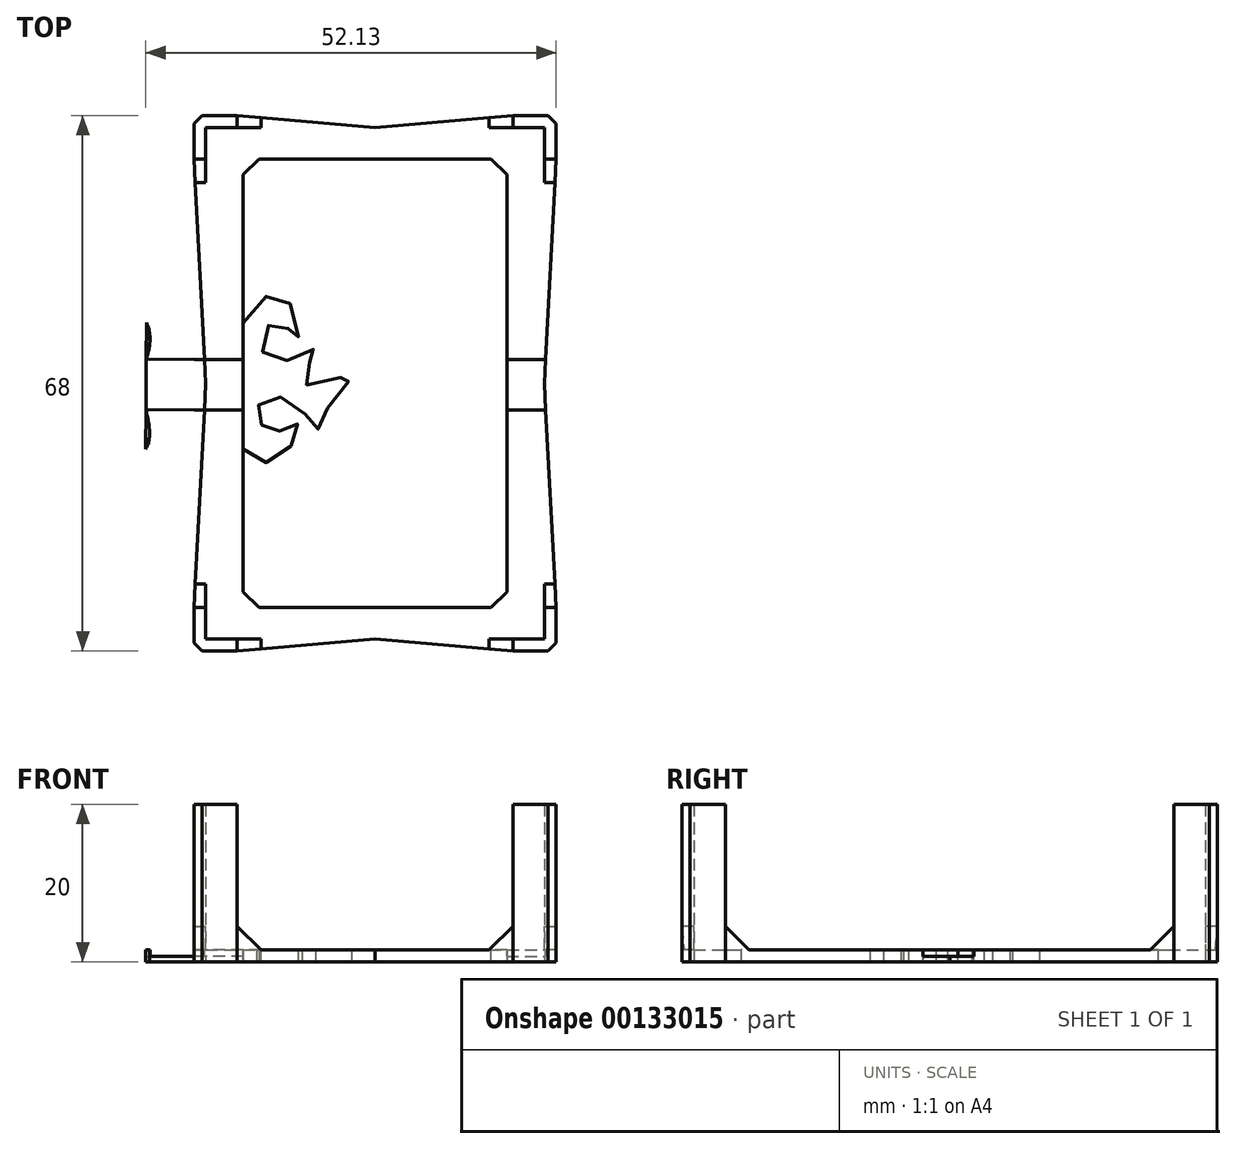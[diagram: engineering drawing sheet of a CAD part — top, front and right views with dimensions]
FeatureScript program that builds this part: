
annotation { "Feature Type Name" : "Feature", "Feature Type Description" : "" }
export const myFeature = defineFeature(function(context is Context, id is Id, definition is map)
    precondition{}
    {
        {
            var Q0;
            Q0=qCreatedBy(makeId("Top.planeOp"),FACE);
            var sketch = newSketch(context, id + "F0", { "sketchPlane" : qUnion([Q0])});
            skLineSegment(sketch, "E0.bottom", {"start": v(21.5, 32.5) * mm, "end": v(17.5, 32.5) * mm});
            skLineSegment(sketch, "E0.top", {"start": v(21.5, -32.5) * mm, "end": v(17.5, -32.5) * mm});
            skLineSegment(sketch, "E0.left", {"start": v(21.5, 32.5) * mm, "end": v(21.5, 28.5) * mm});
            skLineSegment(sketch, "E0.right", {"start": v(-21.5, 32.5) * mm, "end": v(-21.5, 28.5) * mm});
            skLineSegment(sketch, "E1", {"start": v(-17.5, 34) * mm, "end": v(-23, 34) * mm});
            skLineSegment(sketch, "E2", {"start": v(-23, 34) * mm, "end": v(-23, 28.5) * mm});
            skLineSegment(sketch, "E3", {"start": v(-17.5, 32.5) * mm, "end": v(-17.5, 34) * mm});
            skLineSegment(sketch, "E4", {"start": v(-21.5, 28.5) * mm, "end": v(-23, 28.5) * mm});
            skLineSegment(sketch, "E5", {"start": v(17.5, 34) * mm, "end": v(17.5, 32.5) * mm});
            skLineSegment(sketch, "E6", {"start": v(17.5, 34) * mm, "end": v(23, 34) * mm});
            skLineSegment(sketch, "E7", {"start": v(23, 28.5) * mm, "end": v(23, 34) * mm});
            skLineSegment(sketch, "E8", {"start": v(21.5, 28.5) * mm, "end": v(23, 28.5) * mm});
            skLineSegment(sketch, "E9", {"start": v(-23, -28.5) * mm, "end": v(-21.5, -28.5) * mm});
            skLineSegment(sketch, "E10", {"start": v(-23, -28.5) * mm, "end": v(-23, -34) * mm});
            skLineSegment(sketch, "E11", {"start": v(-17.5, -34) * mm, "end": v(-23, -34) * mm});
            skLineSegment(sketch, "E12", {"start": v(-17.5, -32.5) * mm, "end": v(-17.5, -34) * mm});
            skLineSegment(sketch, "E13", {"start": v(17.5, -32.5) * mm, "end": v(17.5, -34) * mm});
            skLineSegment(sketch, "E14", {"start": v(17.5, -34) * mm, "end": v(23, -34) * mm});
            skLineSegment(sketch, "E15", {"start": v(23, -28.5) * mm, "end": v(23, -34) * mm});
            skLineSegment(sketch, "E16", {"start": v(21.5, -28.5) * mm, "end": v(23, -28.5) * mm});
            skLineSegment(sketch, "E17", {"start": v(-16.75, 28.5) * mm, "end": v(16.75, 28.5) * mm});
            skLineSegment(sketch, "E18", {"start": v(16.75, -28.5) * mm, "end": v(-16.75, -28.5) * mm});
            skLineSegment(sketch, "E19", {"start": v(-16.75, 28.5) * mm, "end": v(-16.75, -28.5) * mm});
            skLineSegment(sketch, "E20", {"start": v(16.75, 28.5) * mm, "end": v(16.75, -28.5) * mm});
            skLineSegment(sketch, "E21", {"start": v(-23, 28.5) * mm, "end": v(-21.5, 0) * mm});
            skLineSegment(sketch, "E22", {"start": v(-21.5, 0) * mm, "end": v(-23, -28.5) * mm});
            skLineSegment(sketch, "E23", {"start": v(23, -28.5) * mm, "end": v(21.5, 0) * mm});
            skLineSegment(sketch, "E24", {"start": v(23, 28.5) * mm, "end": v(21.5, 0) * mm});
            skLineSegment(sketch, "E25", {"start": v(-17.5, 34) * mm, "end": v(0, 32.5) * mm});
            skLineSegment(sketch, "E26", {"start": v(0, 32.5) * mm, "end": v(17.5, 34) * mm});
            skLineSegment(sketch, "E27", {"start": v(-17.5, -34) * mm, "end": v(0, -32.5) * mm});
            skLineSegment(sketch, "E28", {"start": v(0, -32.5) * mm, "end": v(17.5, -34) * mm});
            skLineSegment(sketch, "E29.trimOffspring", {"start": v(21.5, -28.5) * mm, "end": v(21.5, -32.5) * mm});
            skLineSegment(sketch, "E30.trimOffspring", {"start": v(-17.5, -32.5) * mm, "end": v(-21.5, -32.5) * mm});
            skLineSegment(sketch, "E31.trimOffspring", {"start": v(-21.5, -28.5) * mm, "end": v(-21.5, -32.5) * mm});
            skLineSegment(sketch, "E32", {"start": v(-17.5, 32.5) * mm, "end": v(-21.5, 32.5) * mm});
            skPoint(sketch, "E33", {"position": v(0, 28.5) * mm});
            skPoint(sketch, "E34", {"position": v(0, -28.5) * mm});
            skPoint(sketch, "E35", {"position": v(-16.75, 0) * mm});
            skPoint(sketch, "E36", {"position": v(16.75, 0) * mm});
            skSolve(sketch);
        }
        {
            var Q0;
            {var subQ0=sQuery(id+"F0.wireOp",EDGE,"E0.left");var subQ3=sQuery(id+"F0.wireOp",EDGE,"E0.bottom");var subQ4=makeQuery(id+"F0.imprint","INTERSECT",VERTEX,{"derivedFrom":[subQ3,subQ0]});Q0=makeQuery(id+"F0.imprint","IMPRINT",FACE,{"disambiguationData":[TD([[makeQuery(id+"F0.imprint","IMPRINT",EDGE,{"disambiguationData":[TD([[subQ4,-1.0]])],"derivedFrom":subQ3}),1.0]])]});}
            var Q1;
            {var subQ0=sQuery(id+"F0.wireOp",EDGE,"E5");Q1=makeQuery(id+"F0.imprint","IMPRINT",FACE,{"disambiguationData":[TD([[makeQuery(id+"F0.imprint","IMPRINT",EDGE,{"derivedFrom":subQ0}),-1.0]])]});}
            var Q2;
            {var subQ4=sQuery(id+"F0.wireOp",EDGE,"E5");Q2=makeQuery(id+"F0.imprint","IMPRINT",FACE,{"disambiguationData":[TD([[makeQuery(id+"F0.imprint","IMPRINT",EDGE,{"derivedFrom":subQ4}),1.0]])]});}
            var Q3;
            {var subQ0=sQuery(id+"F0.wireOp",EDGE,"E8");Q3=makeQuery(id+"F0.imprint","IMPRINT",FACE,{"disambiguationData":[TD([[makeQuery(id+"F0.imprint","IMPRINT",EDGE,{"derivedFrom":subQ0}),-1.0]])]});}
            var Q4;
            {var subQ0=sQuery(id+"F0.wireOp",EDGE,"E16");Q4=makeQuery(id+"F0.imprint","IMPRINT",FACE,{"disambiguationData":[TD([[makeQuery(id+"F0.imprint","IMPRINT",EDGE,{"derivedFrom":subQ0}),1.0]])]});}
            var Q5;
            {var subQ0=sQuery(id+"F0.wireOp",EDGE,"E13");Q5=makeQuery(id+"F0.imprint","IMPRINT",FACE,{"disambiguationData":[TD([[makeQuery(id+"F0.imprint","IMPRINT",EDGE,{"derivedFrom":subQ0}),1.0]])]});}
            var Q6;
            {var subQ0=sQuery(id+"F0.wireOp",EDGE,"E13");Q6=makeQuery(id+"F0.imprint","IMPRINT",FACE,{"disambiguationData":[TD([[makeQuery(id+"F0.imprint","IMPRINT",EDGE,{"derivedFrom":subQ0}),-1.0]])]});}
            var Q7;
            {var subQ0=sQuery(id+"F0.wireOp",EDGE,"E12");Q7=makeQuery(id+"F0.imprint","IMPRINT",FACE,{"disambiguationData":[TD([[makeQuery(id+"F0.imprint","IMPRINT",EDGE,{"derivedFrom":subQ0}),1.0]])]});}
            var Q8;
            {var subQ4=sQuery(id+"F0.wireOp",EDGE,"E9");Q8=makeQuery(id+"F0.imprint","IMPRINT",FACE,{"disambiguationData":[TD([[makeQuery(id+"F0.imprint","IMPRINT",EDGE,{"derivedFrom":subQ4}),-1.0]])]});}
            var Q9;
            {var subQ0=sQuery(id+"F0.wireOp",EDGE,"E9");Q9=makeQuery(id+"F0.imprint","IMPRINT",FACE,{"disambiguationData":[TD([[makeQuery(id+"F0.imprint","IMPRINT",EDGE,{"derivedFrom":subQ0}),1.0]])]});}
            var Q10;
            {var subQ0=sQuery(id+"F0.wireOp",EDGE,"E4");Q10=makeQuery(id+"F0.imprint","IMPRINT",FACE,{"disambiguationData":[TD([[makeQuery(id+"F0.imprint","IMPRINT",EDGE,{"derivedFrom":subQ0}),1.0]])]});}
            var Q11;
            Q11=makeQuery(id+"F0.imprint","IMPRINT",FACE,{"disambiguationData":[TD([[makeQuery(id+"F0.imprint","IMPRINT",EDGE,{"derivedFrom":sQuery(id+"F0.wireOp",EDGE,"E1")}),1.0]])]});
            var Q12;
            {var subQ0=sQuery(id+"F0.wireOp",EDGE,"E3");Q12=makeQuery(id+"F0.imprint","IMPRINT",FACE,{"disambiguationData":[TD([[makeQuery(id+"F0.imprint","IMPRINT",EDGE,{"derivedFrom":subQ0}),-1.0]])]});}
            extrude(context, id + "F1", {"entities" : qUnion([Q0, Q1, Q2, Q3, Q4, Q5, Q6, Q7, Q8, Q9, Q10, Q11, Q12]), "depth" : 1.5 * mm});
        }
        {
            var Q0;
            Q0=makeQuery(id+"F0.imprint","IMPRINT",FACE,{"disambiguationData":[TD([[makeQuery(id+"F0.imprint","IMPRINT",EDGE,{"derivedFrom":sQuery(id+"F0.wireOp",EDGE,"E1")}),1.0]])]});
            var Q1;
            {var subQ4=sQuery(id+"F0.wireOp",EDGE,"E5");Q1=makeQuery(id+"F0.imprint","IMPRINT",FACE,{"disambiguationData":[TD([[makeQuery(id+"F0.imprint","IMPRINT",EDGE,{"derivedFrom":subQ4}),1.0]])]});}
            var Q2;
            {var subQ0=sQuery(id+"F0.wireOp",EDGE,"E13");Q2=makeQuery(id+"F0.imprint","IMPRINT",FACE,{"disambiguationData":[TD([[makeQuery(id+"F0.imprint","IMPRINT",EDGE,{"derivedFrom":subQ0}),1.0]])]});}
            var Q3;
            {var subQ3=sQuery(id+"F0.wireOp",EDGE,"E9");Q3=makeQuery(id+"F0.imprint","IMPRINT",FACE,{"disambiguationData":[TD([[makeQuery(id+"F0.imprint","IMPRINT",EDGE,{"derivedFrom":subQ3}),-1.0]])]});}
            extrude(context, id + "F2", {"entities" : qUnion([Q0, Q1, Q2, Q3]), "operationType" : NewBodyOperationType.ADD, "depth" : 20 * mm});
        }
        {
            var Q0;
            Q0=makeQuery(id+"F2.boolean.opBoolean","INTERSECT",EDGE,{"derivedFrom":[makeQuery(id+"F1.opExtrude","CAP_FACE",FACE,{"disambiguationData":[OSD([sQuery(id+"F0.wireOp",EDGE,"E1"),sQuery(id+"F0.wireOp",EDGE,"E2"),sQuery(id+"F0.wireOp",EDGE,"E6"),sQuery(id+"F0.wireOp",EDGE,"E7"),sQuery(id+"F0.wireOp",EDGE,"E10"),sQuery(id+"F0.wireOp",EDGE,"E11"),sQuery(id+"F0.wireOp",EDGE,"E14"),sQuery(id+"F0.wireOp",EDGE,"E15"),sQuery(id+"F0.wireOp",EDGE,"E17"),sQuery(id+"F0.wireOp",EDGE,"E18"),sQuery(id+"F0.wireOp",EDGE,"E19"),sQuery(id+"F0.wireOp",EDGE,"E20"),sQuery(id+"F0.wireOp",EDGE,"E21"),sQuery(id+"F0.wireOp",EDGE,"E22"),sQuery(id+"F0.wireOp",EDGE,"E23"),sQuery(id+"F0.wireOp",EDGE,"E24"),sQuery(id+"F0.wireOp",EDGE,"E25"),sQuery(id+"F0.wireOp",EDGE,"E26"),sQuery(id+"F0.wireOp",EDGE,"E27"),sQuery(id+"F0.wireOp",EDGE,"E28")])],"isStart":false}),makeQuery(id+"F2.opExtrude","SWEPT_FACE",FACE,{"disambiguationData":[OSD([sQuery(id+"F0.wireOp",EDGE,"E4")])]})]});
            var Q1;
            Q1=makeQuery(id+"F2.boolean.opBoolean","INTERSECT",EDGE,{"derivedFrom":[makeQuery(id+"F1.opExtrude","CAP_FACE",FACE,{"disambiguationData":[OSD([sQuery(id+"F0.wireOp",EDGE,"E1"),sQuery(id+"F0.wireOp",EDGE,"E2"),sQuery(id+"F0.wireOp",EDGE,"E6"),sQuery(id+"F0.wireOp",EDGE,"E7"),sQuery(id+"F0.wireOp",EDGE,"E10"),sQuery(id+"F0.wireOp",EDGE,"E11"),sQuery(id+"F0.wireOp",EDGE,"E14"),sQuery(id+"F0.wireOp",EDGE,"E15"),sQuery(id+"F0.wireOp",EDGE,"E17"),sQuery(id+"F0.wireOp",EDGE,"E18"),sQuery(id+"F0.wireOp",EDGE,"E19"),sQuery(id+"F0.wireOp",EDGE,"E20"),sQuery(id+"F0.wireOp",EDGE,"E21"),sQuery(id+"F0.wireOp",EDGE,"E22"),sQuery(id+"F0.wireOp",EDGE,"E23"),sQuery(id+"F0.wireOp",EDGE,"E24"),sQuery(id+"F0.wireOp",EDGE,"E25"),sQuery(id+"F0.wireOp",EDGE,"E26"),sQuery(id+"F0.wireOp",EDGE,"E27"),sQuery(id+"F0.wireOp",EDGE,"E28")])],"isStart":false}),makeQuery(id+"F2.opExtrude","SWEPT_FACE",FACE,{"disambiguationData":[OSD([sQuery(id+"F0.wireOp",EDGE,"E3")])]})]});
            var Q2;
            Q2=makeQuery(id+"F2.boolean.opBoolean","INTERSECT",EDGE,{"derivedFrom":[makeQuery(id+"F1.opExtrude","CAP_FACE",FACE,{"disambiguationData":[OSD([sQuery(id+"F0.wireOp",EDGE,"E1"),sQuery(id+"F0.wireOp",EDGE,"E2"),sQuery(id+"F0.wireOp",EDGE,"E6"),sQuery(id+"F0.wireOp",EDGE,"E7"),sQuery(id+"F0.wireOp",EDGE,"E10"),sQuery(id+"F0.wireOp",EDGE,"E11"),sQuery(id+"F0.wireOp",EDGE,"E14"),sQuery(id+"F0.wireOp",EDGE,"E15"),sQuery(id+"F0.wireOp",EDGE,"E17"),sQuery(id+"F0.wireOp",EDGE,"E18"),sQuery(id+"F0.wireOp",EDGE,"E19"),sQuery(id+"F0.wireOp",EDGE,"E20"),sQuery(id+"F0.wireOp",EDGE,"E21"),sQuery(id+"F0.wireOp",EDGE,"E22"),sQuery(id+"F0.wireOp",EDGE,"E23"),sQuery(id+"F0.wireOp",EDGE,"E24"),sQuery(id+"F0.wireOp",EDGE,"E25"),sQuery(id+"F0.wireOp",EDGE,"E26"),sQuery(id+"F0.wireOp",EDGE,"E27"),sQuery(id+"F0.wireOp",EDGE,"E28")])],"isStart":false}),makeQuery(id+"F2.opExtrude","SWEPT_FACE",FACE,{"disambiguationData":[OSD([sQuery(id+"F0.wireOp",EDGE,"E8")])]})]});
            var Q3;
            Q3=makeQuery(id+"F2.boolean.opBoolean","INTERSECT",EDGE,{"derivedFrom":[makeQuery(id+"F1.opExtrude","CAP_FACE",FACE,{"disambiguationData":[OSD([sQuery(id+"F0.wireOp",EDGE,"E1"),sQuery(id+"F0.wireOp",EDGE,"E2"),sQuery(id+"F0.wireOp",EDGE,"E6"),sQuery(id+"F0.wireOp",EDGE,"E7"),sQuery(id+"F0.wireOp",EDGE,"E10"),sQuery(id+"F0.wireOp",EDGE,"E11"),sQuery(id+"F0.wireOp",EDGE,"E14"),sQuery(id+"F0.wireOp",EDGE,"E15"),sQuery(id+"F0.wireOp",EDGE,"E17"),sQuery(id+"F0.wireOp",EDGE,"E18"),sQuery(id+"F0.wireOp",EDGE,"E19"),sQuery(id+"F0.wireOp",EDGE,"E20"),sQuery(id+"F0.wireOp",EDGE,"E21"),sQuery(id+"F0.wireOp",EDGE,"E22"),sQuery(id+"F0.wireOp",EDGE,"E23"),sQuery(id+"F0.wireOp",EDGE,"E24"),sQuery(id+"F0.wireOp",EDGE,"E25"),sQuery(id+"F0.wireOp",EDGE,"E26"),sQuery(id+"F0.wireOp",EDGE,"E27"),sQuery(id+"F0.wireOp",EDGE,"E28")])],"isStart":false}),makeQuery(id+"F2.opExtrude","SWEPT_FACE",FACE,{"disambiguationData":[OSD([sQuery(id+"F0.wireOp",EDGE,"E5")])]})]});
            var Q4;
            Q4=makeQuery(id+"F2.boolean.opBoolean","INTERSECT",EDGE,{"derivedFrom":[makeQuery(id+"F1.opExtrude","CAP_FACE",FACE,{"disambiguationData":[OSD([sQuery(id+"F0.wireOp",EDGE,"E1"),sQuery(id+"F0.wireOp",EDGE,"E2"),sQuery(id+"F0.wireOp",EDGE,"E6"),sQuery(id+"F0.wireOp",EDGE,"E7"),sQuery(id+"F0.wireOp",EDGE,"E10"),sQuery(id+"F0.wireOp",EDGE,"E11"),sQuery(id+"F0.wireOp",EDGE,"E14"),sQuery(id+"F0.wireOp",EDGE,"E15"),sQuery(id+"F0.wireOp",EDGE,"E17"),sQuery(id+"F0.wireOp",EDGE,"E18"),sQuery(id+"F0.wireOp",EDGE,"E19"),sQuery(id+"F0.wireOp",EDGE,"E20"),sQuery(id+"F0.wireOp",EDGE,"E21"),sQuery(id+"F0.wireOp",EDGE,"E22"),sQuery(id+"F0.wireOp",EDGE,"E23"),sQuery(id+"F0.wireOp",EDGE,"E24"),sQuery(id+"F0.wireOp",EDGE,"E25"),sQuery(id+"F0.wireOp",EDGE,"E26"),sQuery(id+"F0.wireOp",EDGE,"E27"),sQuery(id+"F0.wireOp",EDGE,"E28")])],"isStart":false}),makeQuery(id+"F2.opExtrude","SWEPT_FACE",FACE,{"disambiguationData":[OSD([sQuery(id+"F0.wireOp",EDGE,"E12")])]})]});
            var Q5;
            Q5=makeQuery(id+"F2.boolean.opBoolean","INTERSECT",EDGE,{"derivedFrom":[makeQuery(id+"F1.opExtrude","CAP_FACE",FACE,{"disambiguationData":[OSD([sQuery(id+"F0.wireOp",EDGE,"E1"),sQuery(id+"F0.wireOp",EDGE,"E2"),sQuery(id+"F0.wireOp",EDGE,"E6"),sQuery(id+"F0.wireOp",EDGE,"E7"),sQuery(id+"F0.wireOp",EDGE,"E10"),sQuery(id+"F0.wireOp",EDGE,"E11"),sQuery(id+"F0.wireOp",EDGE,"E14"),sQuery(id+"F0.wireOp",EDGE,"E15"),sQuery(id+"F0.wireOp",EDGE,"E17"),sQuery(id+"F0.wireOp",EDGE,"E18"),sQuery(id+"F0.wireOp",EDGE,"E19"),sQuery(id+"F0.wireOp",EDGE,"E20"),sQuery(id+"F0.wireOp",EDGE,"E21"),sQuery(id+"F0.wireOp",EDGE,"E22"),sQuery(id+"F0.wireOp",EDGE,"E23"),sQuery(id+"F0.wireOp",EDGE,"E24"),sQuery(id+"F0.wireOp",EDGE,"E25"),sQuery(id+"F0.wireOp",EDGE,"E26"),sQuery(id+"F0.wireOp",EDGE,"E27"),sQuery(id+"F0.wireOp",EDGE,"E28")])],"isStart":false}),makeQuery(id+"F2.opExtrude","SWEPT_FACE",FACE,{"disambiguationData":[OSD([sQuery(id+"F0.wireOp",EDGE,"E9")])]})]});
            var Q6;
            Q6=makeQuery(id+"F2.boolean.opBoolean","INTERSECT",EDGE,{"derivedFrom":[makeQuery(id+"F1.opExtrude","CAP_FACE",FACE,{"disambiguationData":[OSD([sQuery(id+"F0.wireOp",EDGE,"E1"),sQuery(id+"F0.wireOp",EDGE,"E2"),sQuery(id+"F0.wireOp",EDGE,"E6"),sQuery(id+"F0.wireOp",EDGE,"E7"),sQuery(id+"F0.wireOp",EDGE,"E10"),sQuery(id+"F0.wireOp",EDGE,"E11"),sQuery(id+"F0.wireOp",EDGE,"E14"),sQuery(id+"F0.wireOp",EDGE,"E15"),sQuery(id+"F0.wireOp",EDGE,"E17"),sQuery(id+"F0.wireOp",EDGE,"E18"),sQuery(id+"F0.wireOp",EDGE,"E19"),sQuery(id+"F0.wireOp",EDGE,"E20"),sQuery(id+"F0.wireOp",EDGE,"E21"),sQuery(id+"F0.wireOp",EDGE,"E22"),sQuery(id+"F0.wireOp",EDGE,"E23"),sQuery(id+"F0.wireOp",EDGE,"E24"),sQuery(id+"F0.wireOp",EDGE,"E25"),sQuery(id+"F0.wireOp",EDGE,"E26"),sQuery(id+"F0.wireOp",EDGE,"E27"),sQuery(id+"F0.wireOp",EDGE,"E28")])],"isStart":false}),makeQuery(id+"F2.opExtrude","SWEPT_FACE",FACE,{"disambiguationData":[OSD([sQuery(id+"F0.wireOp",EDGE,"E16")])]})]});
            var Q7;
            Q7=makeQuery(id+"F2.boolean.opBoolean","INTERSECT",EDGE,{"derivedFrom":[makeQuery(id+"F1.opExtrude","CAP_FACE",FACE,{"disambiguationData":[OSD([sQuery(id+"F0.wireOp",EDGE,"E1"),sQuery(id+"F0.wireOp",EDGE,"E2"),sQuery(id+"F0.wireOp",EDGE,"E6"),sQuery(id+"F0.wireOp",EDGE,"E7"),sQuery(id+"F0.wireOp",EDGE,"E10"),sQuery(id+"F0.wireOp",EDGE,"E11"),sQuery(id+"F0.wireOp",EDGE,"E14"),sQuery(id+"F0.wireOp",EDGE,"E15"),sQuery(id+"F0.wireOp",EDGE,"E17"),sQuery(id+"F0.wireOp",EDGE,"E18"),sQuery(id+"F0.wireOp",EDGE,"E19"),sQuery(id+"F0.wireOp",EDGE,"E20"),sQuery(id+"F0.wireOp",EDGE,"E21"),sQuery(id+"F0.wireOp",EDGE,"E22"),sQuery(id+"F0.wireOp",EDGE,"E23"),sQuery(id+"F0.wireOp",EDGE,"E24"),sQuery(id+"F0.wireOp",EDGE,"E25"),sQuery(id+"F0.wireOp",EDGE,"E26"),sQuery(id+"F0.wireOp",EDGE,"E27"),sQuery(id+"F0.wireOp",EDGE,"E28")])],"isStart":false}),makeQuery(id+"F2.opExtrude","SWEPT_FACE",FACE,{"disambiguationData":[OSD([sQuery(id+"F0.wireOp",EDGE,"E13")])]})]});
            chamfer(context, id + "F3", {"entities" : qUnion([Q0, Q1, Q2, Q3, Q4, Q5, Q6, Q7]), "width" : 3 * mm, "tangentPropagation" : true});
        }
        {
            var Q0;
            Q0=makeQuery(id+"F1.opExtrude","SWEPT_EDGE",EDGE,{"disambiguationData":[OSD([sQuery(id+"F0.wireOp",EDGE,"E17"),sQuery(id+"F0.wireOp",EDGE,"E19")])]});
            var Q1;
            Q1=makeQuery(id+"F1.opExtrude","SWEPT_EDGE",EDGE,{"disambiguationData":[OSD([sQuery(id+"F0.wireOp",EDGE,"E17"),sQuery(id+"F0.wireOp",EDGE,"E20")])]});
            var Q2;
            Q2=makeQuery(id+"F1.opExtrude","SWEPT_EDGE",EDGE,{"disambiguationData":[OSD([sQuery(id+"F0.wireOp",EDGE,"E18"),sQuery(id+"F0.wireOp",EDGE,"E19")])]});
            var Q3;
            Q3=makeQuery(id+"F1.opExtrude","SWEPT_EDGE",EDGE,{"disambiguationData":[OSD([sQuery(id+"F0.wireOp",EDGE,"E18"),sQuery(id+"F0.wireOp",EDGE,"E20")])]});
            chamfer(context, id + "F4", {"entities" : qUnion([Q0, Q1, Q2, Q3]), "width" : 2 * mm, "tangentPropagation" : true});
        }
        {
            var Q0;
            {var subQ0=sQuery(id+"F0.wireOp",EDGE,"E2");var subQ1=sQuery(id+"F0.wireOp",EDGE,"E1");Q0=makeQuery(id+"F2.boolean.opBoolean","MERGE",EDGE,{"derivedFrom":[makeQuery(id+"F1.opExtrude","SWEPT_EDGE",EDGE,{"disambiguationData":[OSD([subQ1,subQ0])]}),makeQuery(id+"F2.opExtrude","SWEPT_EDGE",EDGE,{"disambiguationData":[OSD([subQ1,subQ0])]})]});}
            var Q1;
            {var subQ0=sQuery(id+"F0.wireOp",EDGE,"E11");var subQ1=sQuery(id+"F0.wireOp",EDGE,"E10");Q1=makeQuery(id+"F2.boolean.opBoolean","MERGE",EDGE,{"derivedFrom":[makeQuery(id+"F1.opExtrude","SWEPT_EDGE",EDGE,{"disambiguationData":[OSD([subQ1,subQ0])]}),makeQuery(id+"F2.opExtrude","SWEPT_EDGE",EDGE,{"disambiguationData":[OSD([subQ1,subQ0])]})]});}
            var Q2;
            {var subQ0=sQuery(id+"F0.wireOp",EDGE,"E15");var subQ1=sQuery(id+"F0.wireOp",EDGE,"E14");Q2=makeQuery(id+"F2.boolean.opBoolean","MERGE",EDGE,{"derivedFrom":[makeQuery(id+"F1.opExtrude","SWEPT_EDGE",EDGE,{"disambiguationData":[OSD([subQ1,subQ0])]}),makeQuery(id+"F2.opExtrude","SWEPT_EDGE",EDGE,{"disambiguationData":[OSD([subQ1,subQ0])]})]});}
            var Q3;
            {var subQ0=sQuery(id+"F0.wireOp",EDGE,"E7");var subQ1=sQuery(id+"F0.wireOp",EDGE,"E6");Q3=makeQuery(id+"F2.boolean.opBoolean","MERGE",EDGE,{"derivedFrom":[makeQuery(id+"F1.opExtrude","SWEPT_EDGE",EDGE,{"disambiguationData":[OSD([subQ1,subQ0])]}),makeQuery(id+"F2.opExtrude","SWEPT_EDGE",EDGE,{"disambiguationData":[OSD([subQ1,subQ0])]})]});}
            chamfer(context, id + "F5", {"entities" : qUnion([Q0, Q1, Q2, Q3]), "width" : 1 * mm, "tangentPropagation" : true});
        }
        {
            var Q0;
            Q0=makeQuery(id+"F1.opExtrude","CAP_FACE",FACE,{"disambiguationData":[OSD([sQuery(id+"F0.wireOp",EDGE,"E1"),sQuery(id+"F0.wireOp",EDGE,"E2"),sQuery(id+"F0.wireOp",EDGE,"E6"),sQuery(id+"F0.wireOp",EDGE,"E7"),sQuery(id+"F0.wireOp",EDGE,"E10"),sQuery(id+"F0.wireOp",EDGE,"E11"),sQuery(id+"F0.wireOp",EDGE,"E14"),sQuery(id+"F0.wireOp",EDGE,"E15"),sQuery(id+"F0.wireOp",EDGE,"E17"),sQuery(id+"F0.wireOp",EDGE,"E18"),sQuery(id+"F0.wireOp",EDGE,"E19"),sQuery(id+"F0.wireOp",EDGE,"E20"),sQuery(id+"F0.wireOp",EDGE,"E21"),sQuery(id+"F0.wireOp",EDGE,"E22"),sQuery(id+"F0.wireOp",EDGE,"E23"),sQuery(id+"F0.wireOp",EDGE,"E24"),sQuery(id+"F0.wireOp",EDGE,"E25"),sQuery(id+"F0.wireOp",EDGE,"E26"),sQuery(id+"F0.wireOp",EDGE,"E27"),sQuery(id+"F0.wireOp",EDGE,"E28")])],"isStart":false});
            var sketch = newSketch(context, id + "F6", { "sketchPlane" : qUnion([Q0])});
            skLineSegment(sketch, "E37", {"start": v(0, 0) * mm, "end": v(-67.35, 0) * mm, "construction": true});
            skLineSegment(sketch, "E38", {"start": v(-23, -28.5) * mm, "end": v(-22.84, 25.5) * mm, "construction": true});
            skLineSegment(sketch, "E39.bottom", {"start": v(-16.75, 3.04) * mm, "end": v(-22.9, 3.04) * mm});
            skLineSegment(sketch, "E39.top", {"start": v(-16.75, -3.39) * mm, "end": v(-22.93, -3.39) * mm});
            skLineSegment(sketch, "E39.left", {"start": v(-16.75, 3.04) * mm, "end": v(-16.75, -0.17) * mm});
            skLineSegment(sketch, "E40", {"start": v(-16.75, -0.17) * mm, "end": v(-16.75, -3.39) * mm});
            skFitSpline(sketch, "E41", {"points": [v(-16.75, 3.04) * mm, v(-16.75, 7.68) * mm, v(-11.73, 11.2) * mm, v(-9.84, 5.5) * mm, v(-12.3, 8) * mm, v(-14.41, 4.39) * mm, v(-10.19, 3.12) * mm, v(-7.48, 4.31) * mm, v(-9.08, 0) * mm, v(-3.07, 1.03) * mm, v(-5.72, -2.62) * mm, v(-7.36, -5.84) * mm, v(-10.45, -2.32) * mm, v(-14.66, -2.56) * mm, v(-14.37, -5.3) * mm, v(-11.92, -6.03) * mm, v(-9.8, -5.22) * mm, v(-12.4, -9.74) * mm, v(-16.75, -8.38) * mm, v(-16.75, -3.39) * mm], "startDerivative": vector(-21.57, 75.62) * mm, "endDerivative": vector(21.75, 96.77) * mm});
            skLineSegment(sketch, "E42", {"start": v(-16.75, 7.68) * mm, "end": v(-16.75, 3.04) * mm});
            skLineSegment(sketch, "E43", {"start": v(-16.75, -3.39) * mm, "end": v(-16.75, -8.38) * mm});
            skFitSpline(sketch, "E44.MirrorCS", {"points": [v(-29.07, 3.08) * mm, v(-29.04, 7.72) * mm, v(-34.04, 11.27) * mm, v(-35.96, 5.57) * mm, v(-33.5, 8.05) * mm, v(-31.4, 4.44) * mm, v(-35.63, 3.2) * mm, v(-38.32, 4.4) * mm, v(-36.75, 0.08) * mm, v(-42.76, 1.15) * mm, v(-40.13, -2.52) * mm, v(-38.5, -5.75) * mm, v(-35.4, -2.25) * mm, v(-31.19, -2.5) * mm, v(-31.5, -5.25) * mm, v(-33.94, -5.97) * mm, v(-36.07, -5.15) * mm, v(-33.48, -9.68) * mm, v(-29.13, -8.34) * mm, v(-29.1, -3.35) * mm], "startDerivative": vector(22, 75.5) * mm, "endDerivative": vector(-21.18, 96.9) * mm});
            skLineSegment(sketch, "E45.MirrorCS", {"start": v(-29.04, 7.72) * mm, "end": v(-29.07, 3.08) * mm});
            skLineSegment(sketch, "E46.MirrorCS", {"start": v(-29.07, 3.08) * mm, "end": v(-22.9, 3.04) * mm});
            skLineSegment(sketch, "E47.MirrorCS", {"start": v(-29.1, -3.35) * mm, "end": v(-22.93, -3.39) * mm});
            skLineSegment(sketch, "E48.MirrorCS", {"start": v(-29.1, -3.35) * mm, "end": v(-29.13, -8.34) * mm});
            skLineSegment(sketch, "E49", {"start": v(-29.07, 3.08) * mm, "end": v(-29.1, -3.35) * mm});
            skSolve(sketch);
        }
        {
            var Q0;
            Q0=makeQuery(id+"F6.imprint","IMPRINT",FACE,{"disambiguationData":[TD([[makeQuery(id+"F6.imprint","IMPRINT",EDGE,{"derivedFrom":sQuery(id+"F6.wireOp",EDGE,"E44.MirrorCS")}),1.0]])]});
            var Q1;
            {var subQ1=sQuery(id+"F6.wireOp",EDGE,"E39.left");Q1=makeQuery(id+"F6.imprint","IMPRINT",FACE,{"disambiguationData":[TD([[makeQuery(id+"F6.imprint","IMPRINT",EDGE,{"derivedFrom":subQ1}),-1.0]])]});}
            var Q2;
            {var subQ1=sQuery(id+"F6.wireOp",EDGE,"E46.MirrorCS");Q2=makeQuery(id+"F6.imprint","IMPRINT",FACE,{"disambiguationData":[TD([[makeQuery(id+"F6.imprint","IMPRINT",EDGE,{"derivedFrom":subQ1}),-1.0]])]});}
            var Q3;
            Q3=makeQuery(id+"F6.imprint","IMPRINT",FACE,{"disambiguationData":[TD([[makeQuery(id+"F6.imprint","IMPRINT",EDGE,{"derivedFrom":sQuery(id+"F6.wireOp",EDGE,"E39.left")}),1.0]])]});
            extrude(context, id + "F7", {"entities" : qUnion([Q0, Q1, Q2, Q3]), "oppositeDirection" : true, "depth" : 1.5 * mm});
        }
        {
            var Q0;
            {var subQ1=sQuery(id+"F6.wireOp",EDGE,"E46.MirrorCS");Q0=makeQuery(id+"F6.imprint","IMPRINT",FACE,{"disambiguationData":[TD([[makeQuery(id+"F6.imprint","IMPRINT",EDGE,{"derivedFrom":subQ1}),-1.0]])]});}
            var Q1;
            {var subQ6=sQuery(id+"F6.wireOp",EDGE,"E39.left");Q1=makeQuery(id+"F6.imprint","IMPRINT",FACE,{"disambiguationData":[TD([[makeQuery(id+"F6.imprint","IMPRINT",EDGE,{"derivedFrom":subQ6}),-1.0]])]});}
            extrude(context, id + "F8", {"entities" : qUnion([Q0, Q1]), "operationType" : NewBodyOperationType.REMOVE, "oppositeDirection" : true, "depth" : .8 * mm});
        }
        {
            var Q0;
            Q0=makeQuery(id+"F6.imprint","IMPRINT",FACE,{"disambiguationData":[TD([[makeQuery(id+"F6.imprint","IMPRINT",EDGE,{"derivedFrom":sQuery(id+"F6.wireOp",EDGE,"E44.MirrorCS")}),1.0]])]});
            var sketch = newSketch(context, id + "F9", { "sketchPlane" : qUnion([Q0])});
            skLineSegment(sketch, "E50.0.0", {"start": v(-21.66, 3.04) * mm, "end": v(-16.75, 3.04) * mm});
            skLineSegment(sketch, "E50.0.1", {"start": v(-16.75, 3.04) * mm, "end": v(-16.75, 7.68) * mm});
            skLineSegment(sketch, "E50.0.2", {"start": v(-16.75, 7.68) * mm, "end": v(-16.75, 26.5) * mm});
            skLineSegment(sketch, "E50.0.3", {"start": v(-16.75, 26.5) * mm, "end": v(-14.75, 28.5) * mm});
            skLineSegment(sketch, "E50.0.4", {"start": v(-14.75, 28.5) * mm, "end": v(14.75, 28.5) * mm});
            skLineSegment(sketch, "E50.0.5", {"start": v(14.75, 28.5) * mm, "end": v(16.75, 26.5) * mm});
            skLineSegment(sketch, "E50.0.6", {"start": v(16.75, 26.5) * mm, "end": v(16.75, -26.5) * mm});
            skLineSegment(sketch, "E50.0.7", {"start": v(16.75, -26.5) * mm, "end": v(14.75, -28.5) * mm});
            skLineSegment(sketch, "E50.0.8", {"start": v(14.75, -28.5) * mm, "end": v(-14.75, -28.5) * mm});
            skLineSegment(sketch, "E50.0.9", {"start": v(-14.75, -28.5) * mm, "end": v(-16.75, -26.5) * mm});
            skLineSegment(sketch, "E50.0.10", {"start": v(-16.75, -26.5) * mm, "end": v(-16.75, -8.38) * mm});
            skLineSegment(sketch, "E50.0.11", {"start": v(-16.75, -8.38) * mm, "end": v(-16.75, -3.39) * mm});
            skLineSegment(sketch, "E50.0.12", {"start": v(-16.75, -3.39) * mm, "end": v(-21.68, -3.39) * mm});
            skLineSegment(sketch, "E50.0.13", {"start": v(-21.68, -3.39) * mm, "end": v(-22.84, -25.5) * mm});
            skLineSegment(sketch, "E50.0.14", {"start": v(-22.84, -25.5) * mm, "end": v(-21.5, -25.5) * mm});
            skLineSegment(sketch, "E50.0.15", {"start": v(-21.5, -25.5) * mm, "end": v(-21.5, -32.5) * mm});
            skLineSegment(sketch, "E50.0.16", {"start": v(-21.5, -32.5) * mm, "end": v(-14.5, -32.5) * mm});
            skLineSegment(sketch, "E50.0.17", {"start": v(-14.5, -32.5) * mm, "end": v(-14.5, -33.74) * mm});
            skLineSegment(sketch, "E50.0.18", {"start": v(-14.5, -33.74) * mm, "end": v(0, -32.5) * mm});
            skLineSegment(sketch, "E50.0.19", {"start": v(0, -32.5) * mm, "end": v(14.5, -33.74) * mm});
            skLineSegment(sketch, "E50.0.20", {"start": v(14.5, -33.74) * mm, "end": v(14.5, -32.5) * mm});
            skLineSegment(sketch, "E50.0.21", {"start": v(14.5, -32.5) * mm, "end": v(21.5, -32.5) * mm});
            skLineSegment(sketch, "E50.0.22", {"start": v(21.5, -32.5) * mm, "end": v(21.5, -25.5) * mm});
            skLineSegment(sketch, "E50.0.23", {"start": v(21.5, -25.5) * mm, "end": v(22.84, -25.5) * mm});
            skLineSegment(sketch, "E50.0.24", {"start": v(22.84, -25.5) * mm, "end": v(21.5, 0) * mm});
            skLineSegment(sketch, "E50.0.25", {"start": v(21.5, 0) * mm, "end": v(22.84, 25.5) * mm});
            skLineSegment(sketch, "E50.0.26", {"start": v(22.84, 25.5) * mm, "end": v(21.5, 25.5) * mm});
            skLineSegment(sketch, "E50.0.27", {"start": v(21.5, 25.5) * mm, "end": v(21.5, 32.5) * mm});
            skLineSegment(sketch, "E50.0.28", {"start": v(21.5, 32.5) * mm, "end": v(14.5, 32.5) * mm});
            skLineSegment(sketch, "E50.0.29", {"start": v(14.5, 32.5) * mm, "end": v(14.5, 33.74) * mm});
            skLineSegment(sketch, "E50.0.30", {"start": v(14.5, 33.74) * mm, "end": v(0, 32.5) * mm});
            skLineSegment(sketch, "E50.0.31", {"start": v(0, 32.5) * mm, "end": v(-14.5, 33.74) * mm});
            skLineSegment(sketch, "E50.0.32", {"start": v(-14.5, 33.74) * mm, "end": v(-14.5, 32.5) * mm});
            skLineSegment(sketch, "E50.0.33", {"start": v(-14.5, 32.5) * mm, "end": v(-21.5, 32.5) * mm});
            skLineSegment(sketch, "E50.0.34", {"start": v(-21.5, 32.5) * mm, "end": v(-21.5, 25.5) * mm});
            skLineSegment(sketch, "E50.0.35", {"start": v(-21.5, 25.5) * mm, "end": v(-22.84, 25.5) * mm});
            skLineSegment(sketch, "E50.0.36", {"start": v(-22.84, 25.5) * mm, "end": v(-21.66, 3.04) * mm});
            skLineSegment(sketch, "E51", {"start": v(16.75, 3.04) * mm, "end": v(21.66, 3.04) * mm});
            skLineSegment(sketch, "E52", {"start": v(16.75, -3.39) * mm, "end": v(21.68, -3.39) * mm});
            skLineSegment(sketch, "E53", {"start": v(16.75, 3.04) * mm, "end": v(16.75, -3.39) * mm});
            skLineSegment(sketch, "E54", {"start": v(21.66, 3.04) * mm, "end": v(21.5, 0) * mm});
            skSolve(sketch);
        }
        {
            var Q0;
            {var subQ6=sQuery(id+"F6.wireOp",EDGE,"E39.left");Q0=makeQuery(id+"F6.imprint","IMPRINT",FACE,{"disambiguationData":[TD([[makeQuery(id+"F6.imprint","IMPRINT",EDGE,{"derivedFrom":subQ6}),-1.0]])]});}
            var Q1;
            Q1=makeQuery(id+"F9.imprint","IMPRINT",FACE,{"disambiguationData":[TD([[makeQuery(id+"F9.imprint","IMPRINT",EDGE,{"derivedFrom":sQuery(id+"F9.wireOp",EDGE,"E51")}),-1.0]])]});
            extrude(context, id + "F10", {"entities" : qUnion([Q0, Q1]), "operationType" : NewBodyOperationType.REMOVE, "oppositeDirection" : true, "depth" : .8 * mm});
        }
    });
